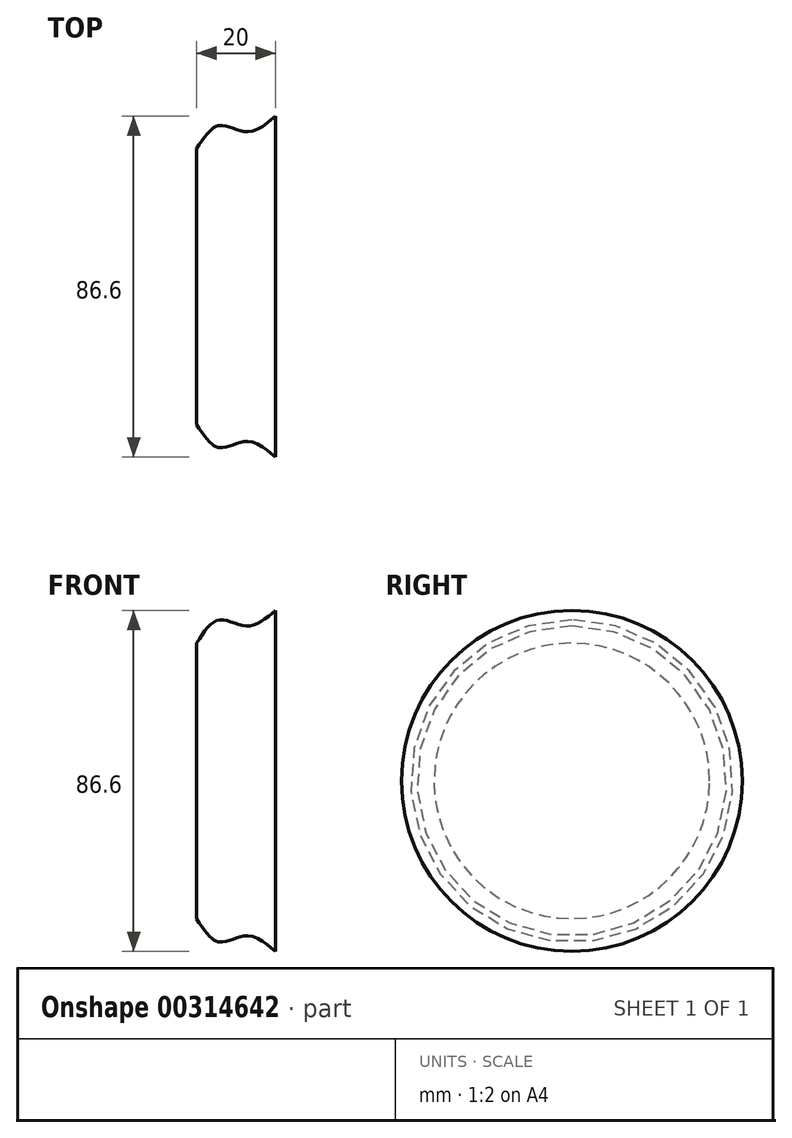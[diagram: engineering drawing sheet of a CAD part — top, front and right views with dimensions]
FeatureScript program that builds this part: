
annotation { "Feature Type Name" : "Feature", "Feature Type Description" : "" }
export const myFeature = defineFeature(function(context is Context, id is Id, definition is map)
    precondition{}
    {
        {
            var Q0;
            Q0=qCreatedBy(makeId("Front.planeOp"),FACE);
            var sketch = newSketch(context, id + "F0", { "sketchPlane" : qUnion([Q0])});
            skLineSegment(sketch, "E0.bottom", {"start": v(21.1, 0) * mm, "end": v(41.1, 0) * mm});
            skLineSegment(sketch, "E0.left", {"start": v(21.1, 0) * mm, "end": v(21.1, 35) * mm});
            skLineSegment(sketch, "E0.right", {"start": v(41.1, 0) * mm, "end": v(41.1, 43.3) * mm});
            skFitSpline(sketch, "E1", {"points": [v(21.1, 35) * mm, v(26.84, 40.9) * mm, v(33.82, 39.35) * mm, v(41.1, 43.3) * mm], "startDerivative": vector(15.39, 24.52) * mm, "endDerivative": vector(20.78, 17.55) * mm});
            skSolve(sketch);
        }
        {
            var Q0;
            Q0 = qSketchRegion(id + "F0", true);
            var Q1;
            Q1=sQuery(id+"F0.wireOp",EDGE,"E0.bottom");
            revolve(context, id + "F1", {"entities" : qUnion([Q0]), "axis" : qUnion([Q1]), "revolveType" : RevolveType.FULL});
        }
    });
